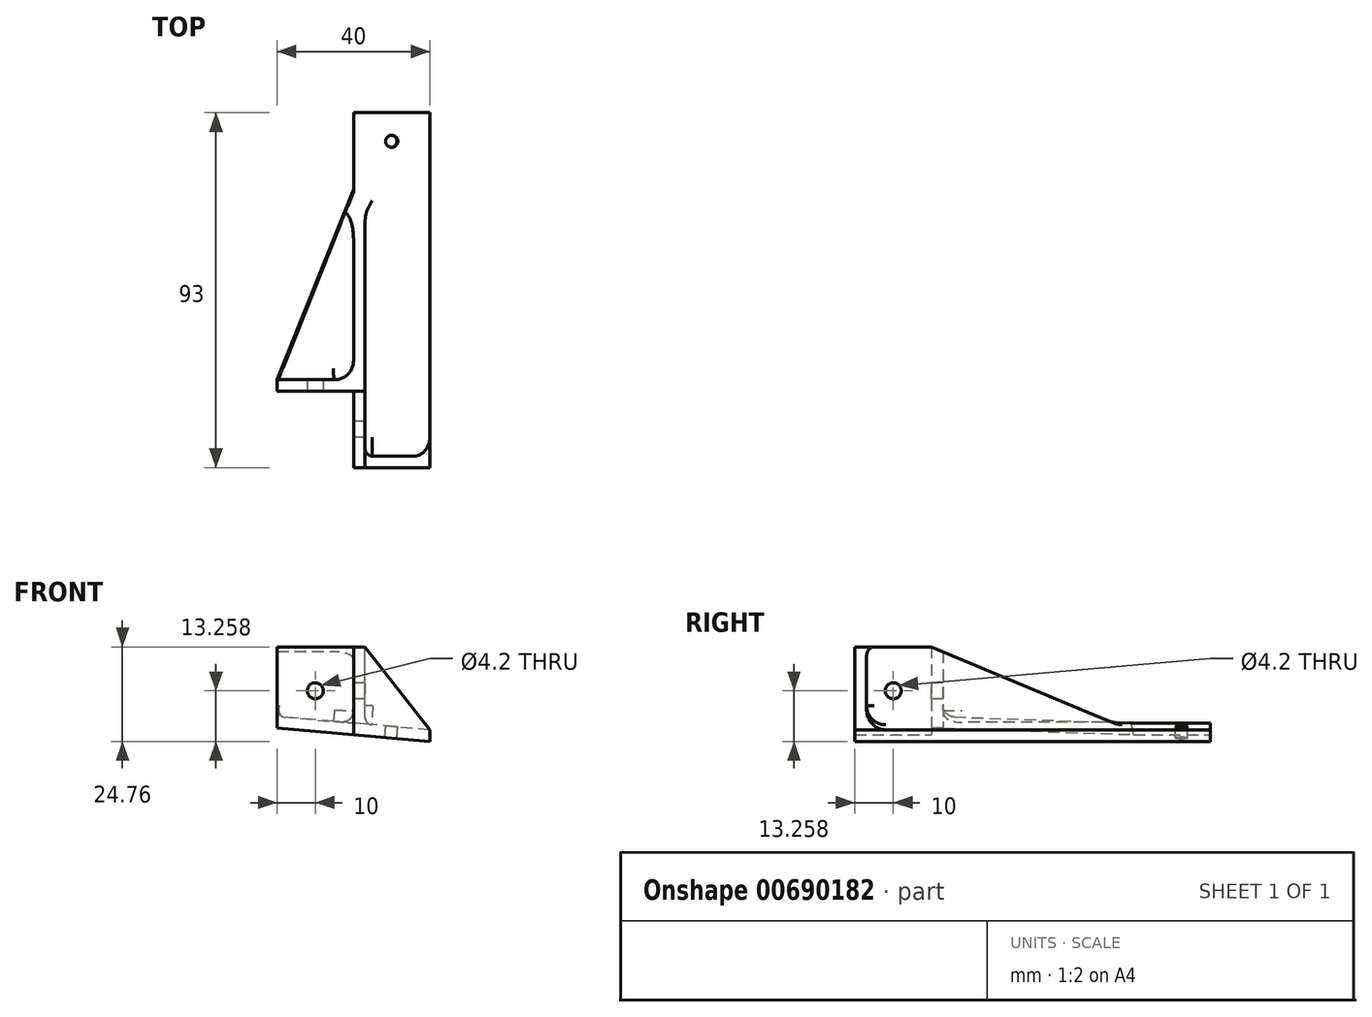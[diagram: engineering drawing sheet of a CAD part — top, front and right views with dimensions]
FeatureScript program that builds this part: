
annotation { "Feature Type Name" : "Feature", "Feature Type Description" : "" }
export const myFeature = defineFeature(function(context is Context, id is Id, definition is map)
    precondition{}
    {
        {
            var Q0;
            Q0=qCreatedBy(makeId("Front.planeOp"),FACE);
            var sketch = newSketch(context, id + "F0", { "sketchPlane" : qUnion([Q0])});
            skLineSegment(sketch, "E0", {"start": v(-261.7, 108.42) * mm, "end": v(-68.52, 91.52) * mm, "construction": true});
            skLineSegment(sketch, "E1", {"start": v(-68.52, 91.52) * mm, "end": v(0, 23) * mm, "construction": true});
            skLineSegment(sketch, "E2", {"start": v(0, 23) * mm, "end": v(2.12, 25.12) * mm, "construction": true});
            skLineSegment(sketch, "E3", {"start": v(2.12, 25.12) * mm, "end": v(-67.18, 94.42) * mm, "construction": true});
            skLineSegment(sketch, "E4", {"start": v(-67.18, 94.42) * mm, "end": v(-261.43, 111.41) * mm, "construction": true});
            skLineSegment(sketch, "E5", {"start": v(-261.43, 111.41) * mm, "end": v(-261.7, 108.42) * mm, "construction": true});
            skLineSegment(sketch, "E6", {"start": v(-249.45, 104.34) * mm, "end": v(-229.45, 102.6) * mm});
            skLineSegment(sketch, "E7", {"start": v(-229.45, 102.6) * mm, "end": v(-229.45, 105.6) * mm});
            skLineSegment(sketch, "E8", {"start": v(-229.45, 105.6) * mm, "end": v(-249.45, 107.35) * mm});
            skLineSegment(sketch, "E9", {"start": v(-249.45, 107.35) * mm, "end": v(-249.45, 104.34) * mm});
            skLineSegment(sketch, "E10", {"start": v(-259.45, 150.5) * mm, "end": v(-259.45, 0) * mm, "construction": true});
            skLineSegment(sketch, "E11", {"start": v(-14.95, 0) * mm, "end": v(-14.95, 151.72) * mm, "construction": true});
            skSolve(sketch);
        }
        {
            var Q0;
            Q0=makeQuery(id+"F0.imprint","IMPRINT",FACE,{"disambiguationData":[TD([[makeQuery(id+"F0.imprint","IMPRINT",EDGE,{"derivedFrom":sQuery(id+"F0.wireOp",EDGE,"E6")}),1.0]])]});
            extrude(context, id + "F1", {"entities" : qUnion([Q0]), "depth" : 93 * mm, "offsetDistance" : 25 * mm});
        }
        {
            var Q0;
            Q0=makeQuery(id+"F1.opExtrude","SWEPT_FACE",FACE,{"disambiguationData":[OSD([sQuery(id+"F0.wireOp",EDGE,"E9")])]});
            var sketch = newSketch(context, id + "F2", { "sketchPlane" : qUnion([Q0])});
            skLineSegment(sketch, "E12.bottom", {"start": v(93, 104.34) * mm, "end": v(18, 104.34) * mm});
            skLineSegment(sketch, "E12.top", {"start": v(93, 127.35) * mm, "end": v(73, 127.35) * mm});
            skLineSegment(sketch, "E12.left", {"start": v(93, 104.34) * mm, "end": v(93, 127.35) * mm});
            skLineSegment(sketch, "E12.right", {"start": v(18, 104.34) * mm, "end": v(73, 127.35) * mm});
            skSolve(sketch);
        }
        {
            var Q0;
            Q0 = qSketchRegion(id + "F2", true);
            extrude(context, id + "F3", {"entities" : qUnion([Q0]), "operationType" : NewBodyOperationType.ADD, "oppositeDirection" : true, "depth" : 3 * mm, "offsetDistance" : 25 * mm});
        }
        {
            var Q0;
            Q0=makeQuery(id+"F3.boolean.opBoolean","MERGE",FACE,{"derivedFrom":[makeQuery(id+"F1.opExtrude","CAP_FACE",FACE,{"disambiguationData":[OSD([sQuery(id+"F0.wireOp",EDGE,"E6"),sQuery(id+"F0.wireOp",EDGE,"E7"),sQuery(id+"F0.wireOp",EDGE,"E8"),sQuery(id+"F0.wireOp",EDGE,"E9")])],"isStart":false}),makeQuery(id+"F3.opExtrude","SWEPT_FACE",FACE,{"disambiguationData":[OSD([sQuery(id+"F2.wireOp",EDGE,"E12.left")])]})]});
            var sketch = newSketch(context, id + "F4", { "sketchPlane" : qUnion([Q0])});
            skLineSegment(sketch, "E13", {"start": v(-246.45, 127.35) * mm, "end": v(-229.45, 105.6) * mm});
            skLineSegment(sketch, "E14", {"start": v(-229.45, 105.6) * mm, "end": v(-229.45, 102.6) * mm});
            skLineSegment(sketch, "E15", {"start": v(-229.45, 102.6) * mm, "end": v(-249.45, 104.34) * mm});
            skLineSegment(sketch, "E16", {"start": v(-249.45, 104.34) * mm, "end": v(-249.45, 127.35) * mm});
            skLineSegment(sketch, "E17", {"start": v(-249.45, 127.35) * mm, "end": v(-246.45, 127.35) * mm});
            skSolve(sketch);
        }
        {
            var Q0;
            Q0 = qSketchRegion(id + "F4", true);
            extrude(context, id + "F5", {"entities" : qUnion([Q0]), "operationType" : NewBodyOperationType.ADD, "oppositeDirection" : true, "depth" : 3 * mm, "offsetDistance" : 25 * mm});
        }
        {
            var Q0;
            Q0=makeQuery(id+"F1.opExtrude","SWEPT_FACE",FACE,{"disambiguationData":[OSD([sQuery(id+"F0.wireOp",EDGE,"E8")])]});
            var sketch = newSketch(context, id + "F6", { "sketchPlane" : qUnion([Q0])});
            skPoint(sketch, "E18", {"position": v(-247.82, -7.5) * mm});
            skPoint(sketch, "E18.positionSnap0", {"position": v(-247.82, 0) * mm});
            skSolve(sketch);
        }
        {
            var Q0;
            Q0=sQuery(id+"F6.wireOp",VERTEX,"E18");
            var Q1;
            Q1=makeQuery(id+"F1.opExtrude","SWEPT_BODY",BODY,{"disambiguationData":[OSD([sQuery(id+"F0.wireOp",EDGE,"E6"),sQuery(id+"F0.wireOp",EDGE,"E7"),sQuery(id+"F0.wireOp",EDGE,"E8"),sQuery(id+"F0.wireOp",EDGE,"E9")])]});
            hole(context, id + "F7", {"style" : HoleStyle.SIMPLE, "endStyle" : HoleEndStyle.BLIND, "holeDiameter" : 3.2 * mm, "majorDiameter" : 5 * mm, "holeDepth" : 5 * mm, "isTappedThrough" : true, "tappedDepth" : 2.3 * mm, "tapClearance" : 3, "startFromSketch" : true, "locations" : qUnion([Q0]), "scope" : qUnion([Q1])});
        }
        {
            var Q0;
            Q0=makeQuery(id+"F3.boolean.opBoolean","MERGE",FACE,{"derivedFrom":[makeQuery(id+"F1.opExtrude","SWEPT_FACE",FACE,{"disambiguationData":[OSD([sQuery(id+"F0.wireOp",EDGE,"E9")])]}),makeQuery(id+"F3.opExtrude","CAP_FACE",FACE,{"disambiguationData":[OSD([sQuery(id+"F2.wireOp",EDGE,"E12.bottom"),sQuery(id+"F2.wireOp",EDGE,"E12.top"),sQuery(id+"F2.wireOp",EDGE,"E12.left"),sQuery(id+"F2.wireOp",EDGE,"E12.right")])],"isStart":true})]});
            var sketch = newSketch(context, id + "F8", { "sketchPlane" : qUnion([Q0])});
            skPoint(sketch, "E19", {"position": v(83, 115.85) * mm});
            skPoint(sketch, "E19.positionSnap0", {"position": v(93, 115.85) * mm});
            skPoint(sketch, "E19.positionSnap1", {"position": v(83, 127.35) * mm});
            skSolve(sketch);
        }
        {
            var Q0;
            Q0=sQuery(id+"F8.wireOp",VERTEX,"E19");
            var Q1;
            Q1=makeQuery(id+"F1.opExtrude","SWEPT_BODY",BODY,{"disambiguationData":[OSD([sQuery(id+"F0.wireOp",EDGE,"E6"),sQuery(id+"F0.wireOp",EDGE,"E7"),sQuery(id+"F0.wireOp",EDGE,"E8"),sQuery(id+"F0.wireOp",EDGE,"E9")])]});
            hole(context, id + "F9", {"style" : HoleStyle.SIMPLE, "endStyle" : HoleEndStyle.BLIND, "holeDiameter" : 4.2 * mm, "majorDiameter" : 5 * mm, "holeDepth" : 5 * mm, "isTappedThrough" : true, "tappedDepth" : 2.3 * mm, "tapClearance" : 3, "startFromSketch" : true, "locations" : qUnion([Q0]), "scope" : qUnion([Q1])});
        }
        {
            var Q0;
            Q0=makeQuery(id+"F5.boolean.opBoolean","INTERSECT",EDGE,{"derivedFrom":[makeQuery(id+"F1.opExtrude","SWEPT_FACE",FACE,{"disambiguationData":[OSD([sQuery(id+"F0.wireOp",EDGE,"E8")])]}),makeQuery(id+"F5.opExtrude","CAP_FACE",FACE,{"disambiguationData":[OSD([sQuery(id+"F4.wireOp",EDGE,"E13"),sQuery(id+"F4.wireOp",EDGE,"E14"),sQuery(id+"F4.wireOp",EDGE,"E15"),sQuery(id+"F4.wireOp",EDGE,"E16"),sQuery(id+"F4.wireOp",EDGE,"E17")])],"isStart":false})]});
            var Q1;
            Q1=makeQuery(id+"F3.boolean.opBoolean","INTERSECT",EDGE,{"derivedFrom":[makeQuery(id+"F1.opExtrude","SWEPT_FACE",FACE,{"disambiguationData":[OSD([sQuery(id+"F0.wireOp",EDGE,"E8")])]}),makeQuery(id+"F3.opExtrude","SWEPT_FACE",FACE,{"disambiguationData":[OSD([sQuery(id+"F2.wireOp",EDGE,"E12.right")])]})]});
            fillet(context, id + "F10", {"entities" : qUnion([Q0, Q1]), "radius" : 5 * mm, "tangentPropagation" : true, "allowEdgeOverflow" : false});
        }
        {
            var Q0;
            Q0=makeQuery(id+"F3.boolean.opBoolean","MERGE",FACE,{"derivedFrom":[makeQuery(id+"F1.opExtrude","SWEPT_FACE",FACE,{"disambiguationData":[OSD([sQuery(id+"F0.wireOp",EDGE,"E9")])]}),makeQuery(id+"F3.opExtrude","CAP_FACE",FACE,{"disambiguationData":[OSD([sQuery(id+"F2.wireOp",EDGE,"E12.bottom"),sQuery(id+"F2.wireOp",EDGE,"E12.top"),sQuery(id+"F2.wireOp",EDGE,"E12.left"),sQuery(id+"F2.wireOp",EDGE,"E12.right")])],"isStart":true})]});
            var sketch = newSketch(context, id + "F11", { "sketchPlane" : qUnion([Q0])});
            skLineSegment(sketch, "E20.bottom", {"start": v(73, 127.35) * mm, "end": v(70, 127.35) * mm});
            skLineSegment(sketch, "E20.top", {"start": v(73, 104.34) * mm, "end": v(70, 104.34) * mm});
            skLineSegment(sketch, "E20.left", {"start": v(73, 127.35) * mm, "end": v(73, 104.34) * mm});
            skLineSegment(sketch, "E20.right", {"start": v(70, 127.35) * mm, "end": v(70, 104.34) * mm});
            skSolve(sketch);
        }
        {
            var Q0;
            {var subQ0=sQuery(id+"F11.wireOp",EDGE,"E20.top");Q0=makeQuery(id+"F11.imprint","IMPRINT",FACE,{"disambiguationData":[TD([[makeQuery(id+"F11.imprint","IMPRINT",EDGE,{"derivedFrom":subQ0}),-1.0]])]});}
            extrude(context, id + "F12", {"entities" : qUnion([Q0]), "operationType" : NewBodyOperationType.ADD, "depth" : 20 * mm, "offsetDistance" : 25 * mm});
        }
        {
            var Q0;
            Q0=makeQuery(id+"F12.opExtrude","SWEPT_FACE",FACE,{"disambiguationData":[OSD([sQuery(id+"F11.wireOp",EDGE,"E20.left")])]});
            var sketch = newSketch(context, id + "F13", { "sketchPlane" : qUnion([Q0])});
            skPoint(sketch, "E21", {"position": v(-259.45, 115.85) * mm});
            skPoint(sketch, "E21.positionSnap0", {"position": v(-269.45, 115.85) * mm});
            skPoint(sketch, "E21.positionSnap1", {"position": v(-259.45, 127.35) * mm});
            skSolve(sketch);
        }
        {
            var Q0;
            Q0=sQuery(id+"F13.wireOp",VERTEX,"E21");
            var Q1;
            Q1=makeQuery(id+"F1.opExtrude","SWEPT_BODY",BODY,{"disambiguationData":[OSD([sQuery(id+"F0.wireOp",EDGE,"E6"),sQuery(id+"F0.wireOp",EDGE,"E7"),sQuery(id+"F0.wireOp",EDGE,"E8"),sQuery(id+"F0.wireOp",EDGE,"E9")])]});
            hole(context, id + "F14", {"style" : HoleStyle.SIMPLE, "endStyle" : HoleEndStyle.BLIND, "holeDiameter" : 4.2 * mm, "majorDiameter" : 5 * mm, "holeDepth" : 5 * mm, "isTappedThrough" : true, "tappedDepth" : 2.3 * mm, "tapClearance" : 3, "startFromSketch" : true, "locations" : qUnion([Q0]), "scope" : qUnion([Q1])});
        }
        {
            var Q0;
            Q0=makeQuery(id+"F12.opExtrude","CAP_EDGE",EDGE,{"disambiguationData":[OSD([sQuery(id+"F11.wireOp",EDGE,"E20.right")])],"isStart":true});
            fillet(context, id + "F15", {"entities" : qUnion([Q0]), "radius" : 5 * mm, "tangentPropagation" : true, "allowEdgeOverflow" : false});
        }
        {
            var Q0;
            Q0=makeQuery(id+"F12.opExtrude","SWEPT_FACE",FACE,{"disambiguationData":[OSD([sQuery(id+"F11.wireOp",EDGE,"E20.left")])]});
            var sketch = newSketch(context, id + "F16", { "sketchPlane" : qUnion([Q0])});
            skLineSegment(sketch, "E22", {"start": v(-269.45, 106.1) * mm, "end": v(-249.45, 104.34) * mm});
            skLineSegment(sketch, "E23", {"start": v(-249.45, 104.34) * mm, "end": v(-269.45, 104.34) * mm});
            skLineSegment(sketch, "E24", {"start": v(-269.45, 104.34) * mm, "end": v(-269.45, 106.1) * mm});
            skSolve(sketch);
        }
        {
            var Q0;
            Q0=makeQuery(id+"F16.imprint","IMPRINT",FACE,{"disambiguationData":[TD([[makeQuery(id+"F16.imprint","IMPRINT",EDGE,{"derivedFrom":sQuery(id+"F16.wireOp",EDGE,"E22")}),-1.0]])]});
            extrude(context, id + "F17", {"entities" : qUnion([Q0]), "operationType" : NewBodyOperationType.REMOVE, "endBound" : BoundingType.UP_TO_NEXT, "oppositeDirection" : true, "depth" : 25 * mm, "offsetDistance" : 25 * mm});
        }
        {
            var Q0;
            Q0=makeQuery(id+"F17.boolean.opBoolean","MERGE",FACE,{"derivedFrom":[makeQuery(id+"F1.opExtrude","SWEPT_FACE",FACE,{"disambiguationData":[OSD([sQuery(id+"F0.wireOp",EDGE,"E6")])]}),makeQuery(id+"F17.opExtrude","SWEPT_FACE",FACE,{"disambiguationData":[OSD([sQuery(id+"F16.wireOp",EDGE,"E22")])]})]});
            var sketch = newSketch(context, id + "F18", { "sketchPlane" : qUnion([Q0])});
            skLineSegment(sketch, "E25", {"start": v(-277.67, 70) * mm, "end": v(-257.6, 20) * mm});
            skLineSegment(sketch, "E26", {"start": v(-257.6, 20) * mm, "end": v(-257.6, 70) * mm});
            skLineSegment(sketch, "E27", {"start": v(-257.6, 70) * mm, "end": v(-277.67, 70) * mm});
            skSolve(sketch);
        }
        {
            var Q0;
            {var subQ0=sQuery(id+"F18.wireOp",EDGE,"E25");Q0=makeQuery(id+"F18.imprint","IMPRINT",FACE,{"disambiguationData":[TD([[makeQuery(id+"F18.imprint","IMPRINT",EDGE,{"derivedFrom":subQ0}),1.0]])]});}
            extrude(context, id + "F19", {"entities" : qUnion([Q0]), "operationType" : NewBodyOperationType.ADD, "oppositeDirection" : true, "depth" : 3 * mm, "offsetDistance" : 25 * mm});
        }
        {
            var Q0;
            {var subQ0=sQuery(id+"F11.wireOp",EDGE,"E20.right");var subQ1=sQuery(id+"F2.wireOp",EDGE,"E12.right");var subQ2=sQuery(id+"F0.wireOp",EDGE,"E8");var subQ3=sQuery(id+"F0.wireOp",EDGE,"E9");Q0=makeQuery(id+"F19.boolean.opBoolean","INTERSECT",EDGE,{"derivedFrom":[makeQuery(id+"F12.boolean.opBoolean","SPLIT",FACE,{"disambiguationData":[TD([makeQuery(id+"F1.opExtrude","SWEPT_FACE",FACE,{"disambiguationData":[OSD([subQ2])]})])],"derivedFrom":makeQuery(id+"F3.boolean.opBoolean","MERGE",FACE,{"derivedFrom":[makeQuery(id+"F1.opExtrude","SWEPT_FACE",FACE,{"disambiguationData":[OSD([subQ3])]}),makeQuery(id+"F3.opExtrude","CAP_FACE",FACE,{"disambiguationData":[OSD([sQuery(id+"F2.wireOp",EDGE,"E12.bottom"),sQuery(id+"F2.wireOp",EDGE,"E12.top"),sQuery(id+"F2.wireOp",EDGE,"E12.left"),subQ1])],"isStart":true})]})}),makeQuery(id+"F19.opExtrude","CAP_FACE",FACE,{"disambiguationData":[OSD([subQ0,sQuery(id+"F16.wireOp",EDGE,"E22"),sQuery(id+"F18.wireOp",EDGE,"E25"),sQuery(id+"F18.wireOp",EDGE,"E26"),sQuery(id+"F18.wireOp",EDGE,"E27")])],"isStart":false})]});}
            fillet(context, id + "F20", {"entities" : qUnion([Q0]), "radius" : 3 * mm, "tangentPropagation" : true, "allowEdgeOverflow" : false});
        }
        {
            var Q0;
            Q0=makeQuery(id+"F3.boolean.opBoolean","INTERSECT",EDGE,{"derivedFrom":[makeQuery(id+"F1.opExtrude","SWEPT_FACE",FACE,{"disambiguationData":[OSD([sQuery(id+"F0.wireOp",EDGE,"E8")])]}),makeQuery(id+"F3.opExtrude","CAP_FACE",FACE,{"disambiguationData":[OSD([sQuery(id+"F2.wireOp",EDGE,"E12.bottom"),sQuery(id+"F2.wireOp",EDGE,"E12.top"),sQuery(id+"F2.wireOp",EDGE,"E12.left"),sQuery(id+"F2.wireOp",EDGE,"E12.right")])],"isStart":false})]});
            fillet(context, id + "F21", {"entities" : qUnion([Q0]), "radius" : 2 * mm, "tangentPropagation" : true, "allowEdgeOverflow" : false});
        }
    });
